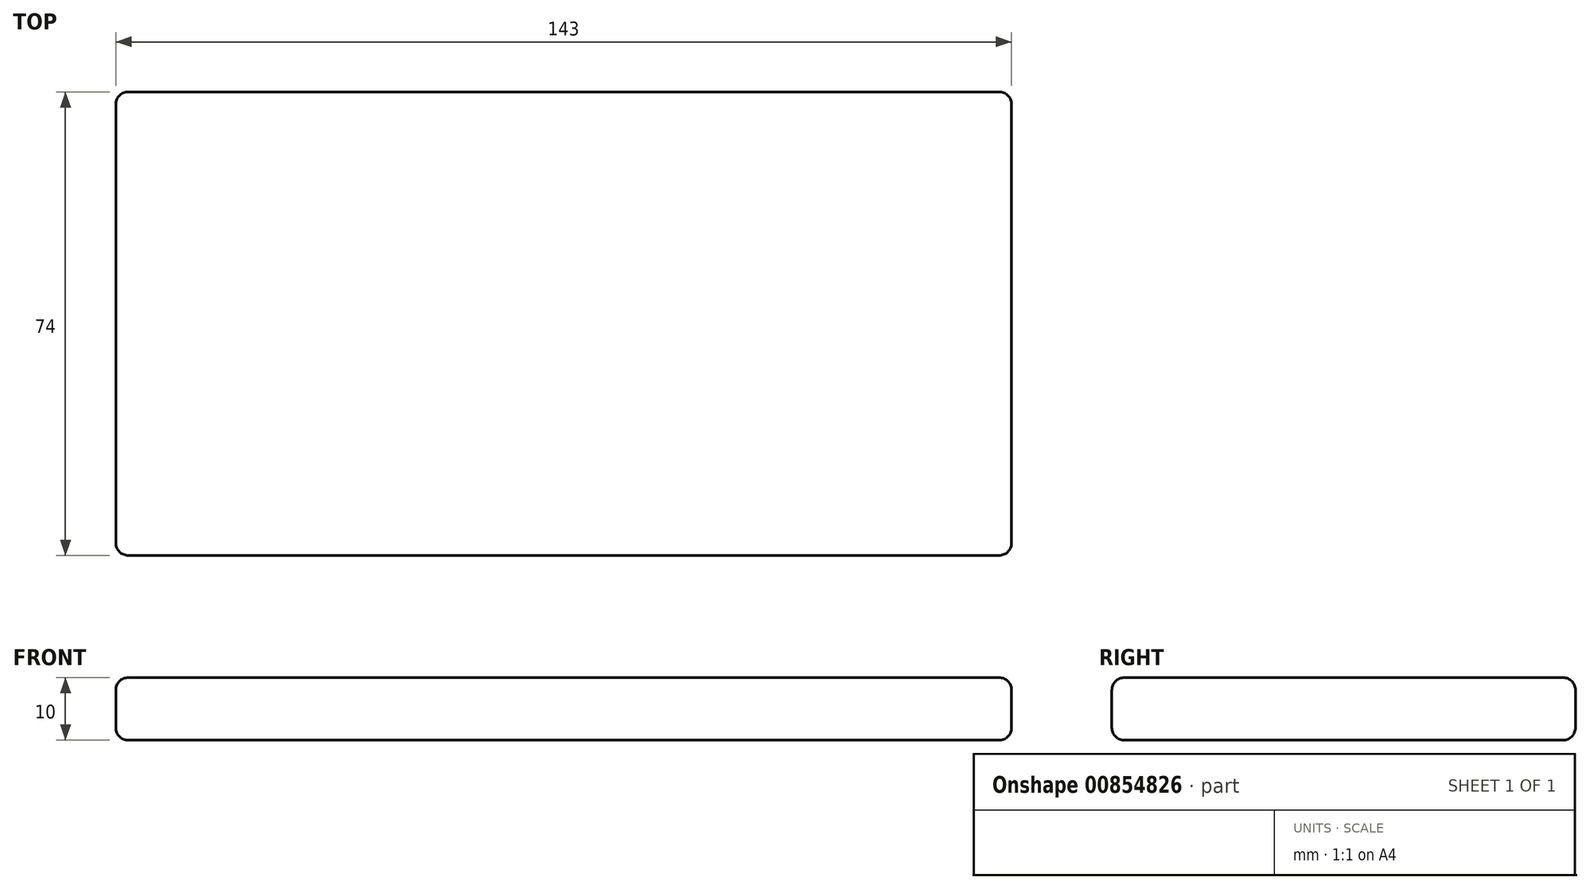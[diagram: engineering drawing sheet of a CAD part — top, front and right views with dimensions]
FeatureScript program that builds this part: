
annotation { "Feature Type Name" : "Feature", "Feature Type Description" : "" }
export const myFeature = defineFeature(function(context is Context, id is Id, definition is map)
    precondition{}
    {
        {
            var Q0;
            Q0=qCreatedBy(makeId("Top.planeOp"),FACE);
            var sketch = newSketch(context, id + "F0", { "sketchPlane" : qUnion([Q0])});
            skLineSegment(sketch, "E0.bottom", {"start": v(-71.5, 37) * mm, "end": v(71.5, 37) * mm});
            skLineSegment(sketch, "E0.top", {"start": v(-71.5, -37) * mm, "end": v(71.5, -37) * mm});
            skLineSegment(sketch, "E0.left", {"start": v(-71.5, 37) * mm, "end": v(-71.5, -37) * mm});
            skLineSegment(sketch, "E0.right", {"start": v(71.5, 37) * mm, "end": v(71.5, -37) * mm});
            skSolve(sketch);
        }
        {
            var Q0;
            Q0 = qSketchRegion(id + "F0", true);
            extrude(context, id + "F1", {"entities" : qUnion([Q0]), "depth" : 10 * mm, "offsetDistance" : 25 * mm});
        }
        {
            var Q0;
            Q0=makeQuery(id+"F1.opExtrude","CAP_EDGE",EDGE,{"disambiguationData":[OSD([sQuery(id+"F0.wireOp",EDGE,"E0.left")])],"isStart":false});
            var Q1;
            Q1=makeQuery(id+"F1.opExtrude","SWEPT_EDGE",EDGE,{"disambiguationData":[OSD([sQuery(id+"F0.wireOp",EDGE,"E0.top"),sQuery(id+"F0.wireOp",EDGE,"E0.left")])]});
            var Q2;
            Q2=makeQuery(id+"F1.opExtrude","CAP_EDGE",EDGE,{"disambiguationData":[OSD([sQuery(id+"F0.wireOp",EDGE,"E0.top")])],"isStart":false});
            var Q3;
            Q3=makeQuery(id+"F1.opExtrude","CAP_EDGE",EDGE,{"disambiguationData":[OSD([sQuery(id+"F0.wireOp",EDGE,"E0.bottom")])],"isStart":false});
            var Q4;
            Q4=makeQuery(id+"F1.opExtrude","CAP_EDGE",EDGE,{"disambiguationData":[OSD([sQuery(id+"F0.wireOp",EDGE,"E0.bottom")])],"isStart":true});
            var Q5;
            Q5=makeQuery(id+"F1.opExtrude","SWEPT_EDGE",EDGE,{"disambiguationData":[OSD([sQuery(id+"F0.wireOp",EDGE,"E0.bottom"),sQuery(id+"F0.wireOp",EDGE,"E0.left")])]});
            var Q6;
            Q6=makeQuery(id+"F1.opExtrude","CAP_EDGE",EDGE,{"disambiguationData":[OSD([sQuery(id+"F0.wireOp",EDGE,"E0.left")])],"isStart":true});
            var Q7;
            Q7=makeQuery(id+"F1.opExtrude","CAP_EDGE",EDGE,{"disambiguationData":[OSD([sQuery(id+"F0.wireOp",EDGE,"E0.top")])],"isStart":true});
            var Q8;
            Q8=makeQuery(id+"F1.opExtrude","CAP_EDGE",EDGE,{"disambiguationData":[OSD([sQuery(id+"F0.wireOp",EDGE,"E0.right")])],"isStart":true});
            var Q9;
            Q9=makeQuery(id+"F1.opExtrude","SWEPT_EDGE",EDGE,{"disambiguationData":[OSD([sQuery(id+"F0.wireOp",EDGE,"E0.top"),sQuery(id+"F0.wireOp",EDGE,"E0.right")])]});
            var Q10;
            Q10=makeQuery(id+"F1.opExtrude","SWEPT_EDGE",EDGE,{"disambiguationData":[OSD([sQuery(id+"F0.wireOp",EDGE,"E0.bottom"),sQuery(id+"F0.wireOp",EDGE,"E0.right")])]});
            var Q11;
            Q11=makeQuery(id+"F1.opExtrude","CAP_EDGE",EDGE,{"disambiguationData":[OSD([sQuery(id+"F0.wireOp",EDGE,"E0.right")])],"isStart":false});
            fillet(context, id + "F2", {"entities" : qUnion([Q0, Q1, Q2, Q3, Q4, Q5, Q6, Q7, Q8, Q9, Q10, Q11]), "radius" : 2 * mm, "tangentPropagation" : true, "allowEdgeOverflow" : false});
        }
    });
